FCSTD DOCUMENT  (FreeCAD 0.16R6712 (Git))
Label: Держатель индикатора
License: All rights reserved
LicenseURL: http://en.wikipedia.org/wiki/All_rights_reserved
objects: Sketcher::SketchObject×4, PartDesign::Pocket×4, PartDesign::Fillet×2, Part::Box×1
note: 15 computed .brp shape members not serialized (recipe doc carries the construction recipe); baked Part::Feature solids carry a one-line shape summary decoded from their .brp

FEATURE [Part::Box] Box  label="Куб"
  Height = 10
  Length = 40
  Width = 16
FEATURE [Sketcher::SketchObject] Sketch
  ExternalGeometry = -> [Box]
  Placement = pos=(0,0,10) rot=(0,0,1;0rad)
  Support = -> Pocket003 [Face11]
  sketch-geometry (11):
    g0: LineSegment [constr] StartX=0 StartY=8 StartZ=0 EndX=40.0548 EndY=8 EndZ=0
    g1: LineSegment [constr] StartX=28 StartY=11.5941 StartZ=0 EndX=28 EndY=4.43678 EndZ=0
    g2: Circle CenterX=28 CenterY=8 CenterZ=0 NormalX=0 NormalY=0 NormalZ=1 Radius=4
    g3: LineSegment StartX=12.0039 StartY=11 StartZ=0 EndX=-1.03375 EndY=11 EndZ=0
    g4: LineSegment StartX=-1.03375 StartY=11 StartZ=0 EndX=-1.03375 EndY=16.6291 EndZ=0
    g5: LineSegment StartX=-1.03375 StartY=16.6291 StartZ=0 EndX=12.0039 EndY=16.6291 EndZ=0
    g6: LineSegment StartX=12.0039 StartY=16.6291 StartZ=0 EndX=12.0039 EndY=11 EndZ=0
    g7: LineSegment StartX=12.0039 StartY=5 StartZ=0 EndX=-1.51921 EndY=5 EndZ=0
    g8: LineSegment StartX=-1.51921 StartY=5 StartZ=0 EndX=-1.51921 EndY=-1.0206 EndZ=0
    g9: LineSegment StartX=-1.51921 StartY=-1.0206 StartZ=0 EndX=12.0039 EndY=-1.0206 EndZ=0
    g10: LineSegment StartX=12.0039 StartY=-1.0206 StartZ=0 EndX=12.0039 EndY=5 EndZ=0
  constraints (26):
    c: PointOnObject(g0,g-2)
    c: Horizontal(g0)
    c: Vertical(g1)
    c: PointOnObject(g2,g0)
    c: Radius(g2) = 4
    c: Coincident(g3,g4)
    c: Coincident(g4,g5)
    c: Coincident(g5,g6)
    c: Coincident(g6,g3)
    c: Horizontal(g3)
    c: Horizontal(g5)
    c: Vertical(g4)
    c: Vertical(g6)
    c: Coincident(g7,g8)
    c: Coincident(g8,g9)
    c: Coincident(g9,g10)
    c: Coincident(g10,g7)
    c: Horizontal(g7)
    c: Horizontal(g9)
    c: Vertical(g8)
    c: Vertical(g10)
    c: DistanceY(g0,g-3) = 8
    c: DistanceX(g1,g-3) = 12
    c: PointOnObject(g2,g1)
    c: Symmetric(g3,g7,g0)
    c: DistanceY(g7,g3) = 6
FEATURE [Sketcher::SketchObject] Sketch001
  ExternalGeometry = -> [Box]
  Placement = pos=(0,16,0) rot=(0,0.707107,0.707107;3.14159rad)
  Support = -> Pocket [Face7]
  sketch-geometry (3):
    g0: LineSegment [constr] StartX=-40 StartY=5 StartZ=0 EndX=-0.024146 EndY=5 EndZ=0
    g1: LineSegment [constr] StartX=-36 StartY=7.72836 StartZ=0 EndX=-36 EndY=2.44337 EndZ=0
    g2: Circle CenterX=-36 CenterY=5 CenterZ=0 NormalX=0 NormalY=0 NormalZ=1 Radius=1.54702
  constraints (8):
    c: PointOnObject(g0,g-3)
    c: Horizontal(g0)
    c: DistanceY(g0,g-3) = 5
    c: Vertical(g1)
    c: DistanceX(g1,g-3) = -4
    c: PointOnObject(g2,g0)
    c: Radius(g2) = 1.54702
    c: PointOnObject(g2,g1)
FEATURE [PartDesign::Pocket] Pocket
  Length = 5
  Sketch = -> Sketch
  Type = 1
FEATURE [PartDesign::Pocket] Pocket001
  Length = 5
  Sketch = -> Sketch001
  Type = 1
FEATURE [Sketcher::SketchObject] Sketch002
  ExternalGeometry = -> [Pocket001]
  Placement = pos=(0,0,0) rot=(1,0,0;3.14159rad)
  Support = -> Pocket001 [Face4]
  sketch-geometry (5):
    g0: LineSegment StartX=40.6243 StartY=-6.5 StartZ=0 EndX=16.5232 EndY=-6.5 EndZ=0
    g1: LineSegment StartX=16.5232 StartY=-6.5 StartZ=0 EndX=16.5232 EndY=-9.5 EndZ=0
    g2: LineSegment StartX=16.5232 StartY=-9.5 StartZ=0 EndX=40.6243 EndY=-9.5 EndZ=0
    g3: LineSegment StartX=40.6243 StartY=-9.5 StartZ=0 EndX=40.6243 EndY=-6.5 EndZ=0
    g4: LineSegment [constr] StartX=16.5232 StartY=-8 StartZ=0 EndX=40 EndY=-8 EndZ=0
  constraints (14):
    c: Coincident(g0,g1)
    c: Coincident(g1,g2)
    c: Coincident(g2,g3)
    c: Coincident(g3,g0)
    c: Horizontal(g0)
    c: Horizontal(g2)
    c: Vertical(g1)
    c: Vertical(g3)
    c: PointOnObject(g4,g1)
    c: PointOnObject(g4,g-3)
    c: Horizontal(g4)
    c: Symmetric(g0,g1,g4)
    c: Symmetric(g-3,g-3,g4)
    c: DistanceY(g2,g0) = 3
FEATURE [PartDesign::Pocket] Pocket002
  Length = 5
  Sketch = -> Sketch002
  Type = 1
FEATURE [PartDesign::Fillet] Fillet
  Base = -> Pocket002 [Edge3,Edge1]
  Radius = 4.5
FEATURE [Sketcher::SketchObject] Sketch003
  ExternalGeometry = -> [Fillet]
  Placement = pos=(0,5,0) rot=(1,0,0;1.5708rad)
  Support = -> Fillet [Face5]
  sketch-geometry (2):
    g0: LineSegment [constr] StartX=12.0039 StartY=5 StartZ=0 EndX=0.574409 EndY=5 EndZ=0
    g1: Circle CenterX=4.5 CenterY=5 CenterZ=0 NormalX=0 NormalY=0 NormalZ=1 Radius=1.52271
  constraints (5):
    c: PointOnObject(g0,g-3)
    c: Horizontal(g0)
    c: Symmetric(g-3,g-3,g0)
    c: PointOnObject(g1,g0)
    c: DistanceX(g1) = 4.5
FEATURE [PartDesign::Pocket] Pocket003
  Length = 5
  Sketch = -> Sketch003
  Type = 1
FEATURE [PartDesign::Fillet] Fillet001
  Base = -> Pocket003 [Edge51,Edge48]
  Radius = 2
